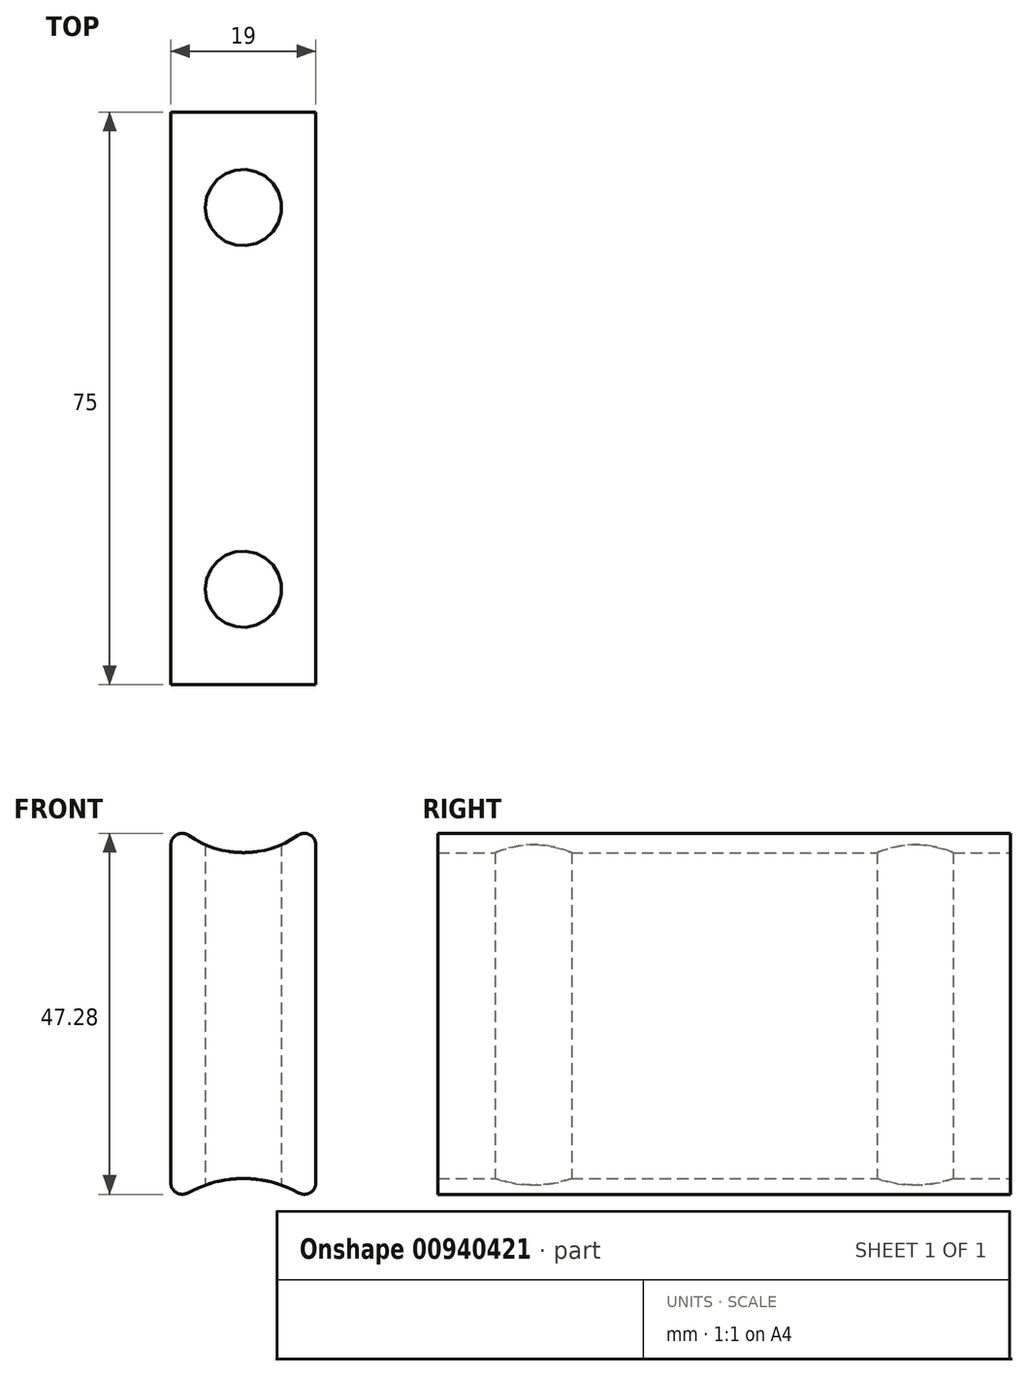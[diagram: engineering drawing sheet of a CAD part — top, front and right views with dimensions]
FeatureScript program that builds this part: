
annotation { "Feature Type Name" : "Feature", "Feature Type Description" : "" }
export const myFeature = defineFeature(function(context is Context, id is Id, definition is map)
    precondition{}
    {
        {
            var Q0;
            Q0=qCreatedBy(makeId("Front.planeOp"),FACE);
            var sketch = newSketch(context, id + "F0", { "sketchPlane" : qUnion([Q0])});
            skArc(sketch, "E0", {"start": v(-7.14, 59.94) * mm, "mid": v(0, 57.7) * mm, "end": v(7.14, 59.94) * mm});
            skArc(sketch, "E1", {"start": v(7.27, 13.12) * mm, "mid": v(0, 15) * mm, "end": v(-7.27, 13.12) * mm});
            skLineSegment(sketch, "E2", {"start": v(-9.5, 58.71) * mm, "end": v(-9.5, 14.43) * mm});
            skLineSegment(sketch, "E3", {"start": v(9.5, 58.71) * mm, "end": v(9.5, 14.43) * mm});
            skPoint(sketch, "E4.visualSharp", {"position": v(-9.5, 62.08) * mm});
            skArc(sketch, "E4.filletArc", {"start": v(-7.14, 59.94) * mm, "mid": v(-8.7, 60.04) * mm, "end": v(-9.5, 58.71) * mm});
            skPoint(sketch, "E5.visualSharp", {"position": v(9.5, 62.08) * mm});
            skArc(sketch, "E5.filletArc", {"start": v(9.5, 58.71) * mm, "mid": v(8.7, 60.04) * mm, "end": v(7.14, 59.94) * mm});
            skPoint(sketch, "E6.visualSharp", {"position": v(-9.5, 11.6) * mm});
            skArc(sketch, "E6.filletArc", {"start": v(-9.5, 14.43) * mm, "mid": v(-8.76, 13.14) * mm, "end": v(-7.27, 13.12) * mm});
            skPoint(sketch, "E7.visualSharp", {"position": v(9.5, 11.6) * mm});
            skArc(sketch, "E7.filletArc", {"start": v(7.27, 13.12) * mm, "mid": v(8.76, 13.14) * mm, "end": v(9.5, 14.43) * mm});
            skSolve(sketch);
        }
        {
            var Q0;
            Q0 = qSketchRegion(id + "F0", true);
            extrude(context, id + "F1", {"entities" : qUnion([Q0]), "endBound" : BoundingType.SYMMETRIC, "depth" : 75 * mm, "offsetDistance" : 25 * mm});
        }
        {
            var Q0;
            Q0=qCreatedBy(makeId("Top.planeOp"),FACE);
            var sketch = newSketch(context, id + "F2", { "sketchPlane" : qUnion([Q0])});
            skCircle(sketch, "E8", {"center": v(0, 25) * mm, "radius": 5 * mm});
            skCircle(sketch, "E9", {"center": v(0, -25) * mm, "radius": 5 * mm});
            skSolve(sketch);
        }
        {
            var Q0;
            Q0 = qSketchRegion(id + "F2", true);
            extrude(context, id + "F3", {"entities" : qUnion([Q0]), "operationType" : NewBodyOperationType.REMOVE, "depth" : 103.7 * mm, "offsetDistance" : 25 * mm});
        }
    });
